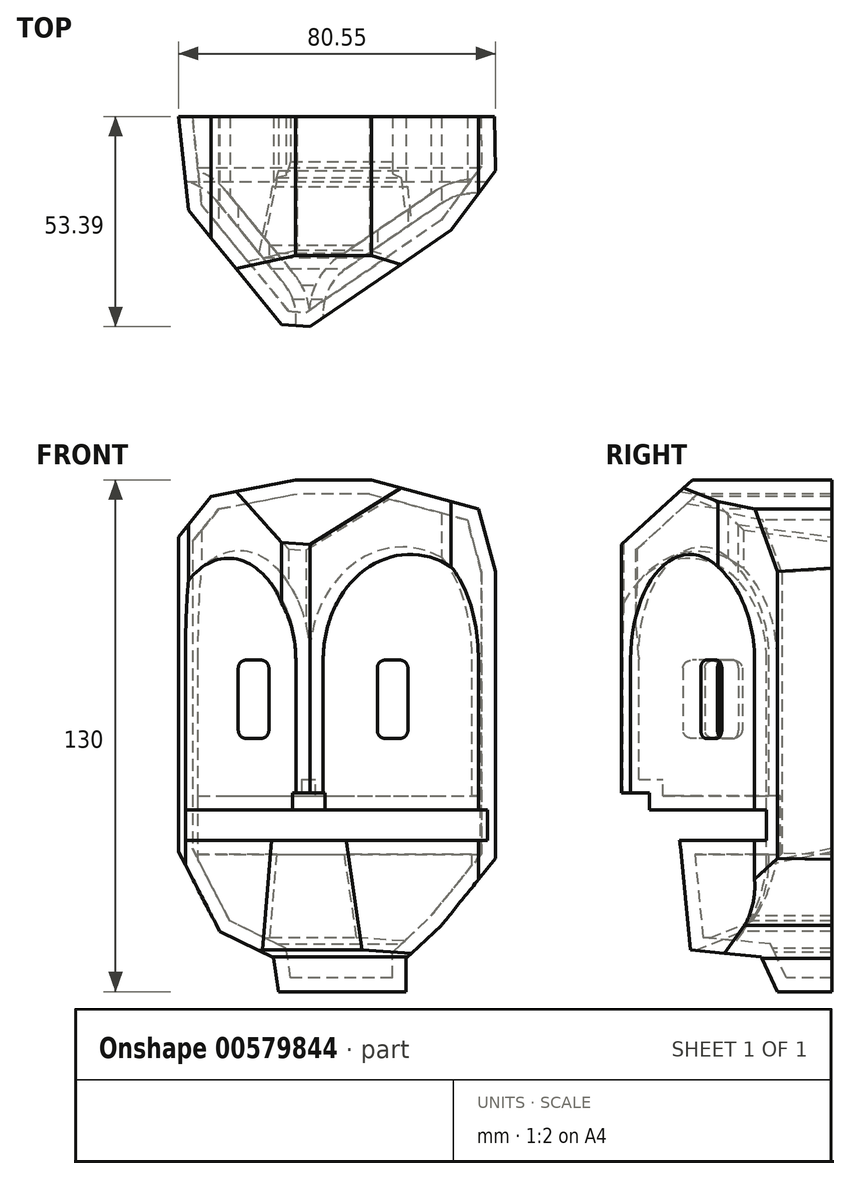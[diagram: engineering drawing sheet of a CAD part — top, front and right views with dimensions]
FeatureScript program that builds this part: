
annotation { "Feature Type Name" : "Feature", "Feature Type Description" : "" }
export const myFeature = defineFeature(function(context is Context, id is Id, definition is map)
    precondition{}
    {
        {
            var Q0;
            Q0=qCreatedBy(makeId("Top.planeOp"),FACE);
            var sketch = newSketch(context, id + "F0", { "sketchPlane" : qUnion([Q0])});
            skLineSegment(sketch, "E0", {"start": v(-31.31, 115.93) * mm, "end": v(-28.8, 92.1) * mm});
            skLineSegment(sketch, "E1", {"start": v(-28.8, 92.1) * mm, "end": v(-5.08, 63.06) * mm});
            skLineSegment(sketch, "E2", {"start": v(-5.08, 63.06) * mm, "end": v(2.1, 62.54) * mm});
            skLineSegment(sketch, "E3", {"start": v(2.1, 62.54) * mm, "end": v(37.94, 87.04) * mm});
            skLineSegment(sketch, "E4", {"start": v(37.94, 87.04) * mm, "end": v(49.24, 102.15) * mm});
            skLineSegment(sketch, "E5", {"start": v(49.24, 102.15) * mm, "end": v(49, 115.93) * mm});
            skLineSegment(sketch, "E6", {"start": v(49, 115.93) * mm, "end": v(-31.31, 115.93) * mm});
            skSolve(sketch);
        }
        {
            var Q0;
            Q0 = qSketchRegion(id + "F0", true);
            extrude(context, id + "F1", {"entities" : qUnion([Q0]), "depth" : 130 * mm, "offsetDistance" : 25 * mm});
        }
        {
            var Q0;
            Q0=makeQuery(id+"F1.opExtrude","SWEPT_FACE",FACE,{"disambiguationData":[OSD([sQuery(id+"F0.wireOp",EDGE,"E3")])]});
            cPlane(context, id + "F2", {"entities" : qUnion([Q0]), "cplaneType" : CPlaneType.OFFSET, "offset" : 13 * mm, "width" : 150 * mm, "height" : 150 * mm});
        }
        {
            var Q0;
            Q0=qCreatedBy(id+"F2.planeOp",FACE);
            var sketch = newSketch(context, id + "F3", { "sketchPlane" : qUnion([Q0])});
            skArc(sketch, "E7", {"start": v(96.46, 84.36) * mm, "mid": v(67.84, 112.98) * mm, "end": v(39.22, 84.36) * mm});
            skLineSegment(sketch, "E8", {"start": v(39.22, -2) * mm, "end": v(39.22, 84.36) * mm});
            skLineSegment(sketch, "E9", {"start": v(96.46, 84.36) * mm, "end": v(96.46, -2) * mm});
            skLineSegment(sketch, "E10", {"start": v(96.46, -2) * mm, "end": v(39.22, -2) * mm});
            skSolve(sketch);
        }
        {
            var Q0;
            Q0 = qSketchRegion(id + "F3", true);
            extrude(context, id + "F4", {"entities" : qUnion([Q0]), "oppositeDirection" : true, "depth" : 20 * mm, "offsetDistance" : 25 * mm});
        }
        {
            var Q0;
            Q0=makeQuery(id+"F4.opExtrude","CAP_EDGE",EDGE,{"disambiguationData":[OSD([sQuery(id+"F3.wireOp",EDGE,"E8")])],"isStart":false});
            fillet(context, id + "F5", {"entities" : qUnion([Q0]), "radius" : 14 * mm, "tangentPropagation" : true, "allowEdgeOverflow" : false});
        }
        {
            var Q0;
            Q0=makeQuery(id+"F4.opExtrude","SWEPT_BODY",BODY,{"disambiguationData":[OSD([sQuery(id+"F3.wireOp",EDGE,"E7"),sQuery(id+"F3.wireOp",EDGE,"E8"),sQuery(id+"F3.wireOp",EDGE,"E9"),sQuery(id+"F3.wireOp",EDGE,"E10")])]});
            var Q1;
            Q1=makeQuery(id+"F1.opExtrude","SWEPT_BODY",BODY,{"disambiguationData":[OSD([sQuery(id+"F0.wireOp",EDGE,"E0"),sQuery(id+"F0.wireOp",EDGE,"E1"),sQuery(id+"F0.wireOp",EDGE,"E2"),sQuery(id+"F0.wireOp",EDGE,"E3"),sQuery(id+"F0.wireOp",EDGE,"E4"),sQuery(id+"F0.wireOp",EDGE,"E5"),sQuery(id+"F0.wireOp",EDGE,"E6")])]});
            booleanBodies(context, id + "F6", {"operationType" : BooleanOperationType.SUBTRACTION, "tools" : qUnion([Q0]), "targets" : qUnion([Q1])});
        }
        {
            var Q0;
            Q0=makeQuery(id+"F1.opExtrude","SWEPT_FACE",FACE,{"disambiguationData":[OSD([sQuery(id+"F0.wireOp",EDGE,"E1")])]});
            cPlane(context, id + "F7", {"entities" : qUnion([Q0]), "cplaneType" : CPlaneType.OFFSET, "offset" : 13 * mm, "width" : 150 * mm, "height" : 150 * mm});
        }
        {
            var Q0;
            Q0=qCreatedBy(id+"F7.planeOp",FACE);
            var sketch = newSketch(context, id + "F8", { "sketchPlane" : qUnion([Q0])});
            skPoint(sketch, "E11.0", {"position": v(-31.54, 84.36) * mm});
            skArc(sketch, "E12", {"start": v(-45.8, 84.36) * mm, "mid": v(-73.43, 112) * mm, "end": v(-101.06, 84.36) * mm});
            skLineSegment(sketch, "E13", {"start": v(-101.06, -2) * mm, "end": v(-101.06, 84.36) * mm});
            skLineSegment(sketch, "E14", {"start": v(-45.8, 84.36) * mm, "end": v(-45.8, -2) * mm});
            skLineSegment(sketch, "E15", {"start": v(-45.8, -2) * mm, "end": v(-101.06, -2) * mm});
            skSolve(sketch);
        }
        {
            var Q0;
            Q0 = qSketchRegion(id + "F8", true);
            extrude(context, id + "F9", {"entities" : qUnion([Q0]), "oppositeDirection" : true, "depth" : 20 * mm, "offsetDistance" : 25 * mm});
        }
        {
            var Q0;
            Q0=makeQuery(id+"F9.opExtrude","CAP_EDGE",EDGE,{"disambiguationData":[OSD([sQuery(id+"F8.wireOp",EDGE,"E12")])],"isStart":false});
            fillet(context, id + "F10", {"entities" : qUnion([Q0]), "radius" : 14 * mm, "tangentPropagation" : true, "allowEdgeOverflow" : false});
        }
        {
            var Q0;
            Q0=makeQuery(id+"F9.opExtrude","SWEPT_BODY",BODY,{"disambiguationData":[OSD([sQuery(id+"F8.wireOp",EDGE,"E12"),sQuery(id+"F8.wireOp",EDGE,"E13"),sQuery(id+"F8.wireOp",EDGE,"E14"),sQuery(id+"F8.wireOp",EDGE,"E15")])]});
            var Q1;
            Q1=makeQuery(id+"F1.opExtrude","SWEPT_BODY",BODY,{"disambiguationData":[OSD([sQuery(id+"F0.wireOp",EDGE,"E0"),sQuery(id+"F0.wireOp",EDGE,"E1"),sQuery(id+"F0.wireOp",EDGE,"E2"),sQuery(id+"F0.wireOp",EDGE,"E3"),sQuery(id+"F0.wireOp",EDGE,"E4"),sQuery(id+"F0.wireOp",EDGE,"E5"),sQuery(id+"F0.wireOp",EDGE,"E6")])]});
            booleanBodies(context, id + "F11", {"operationType" : BooleanOperationType.SUBTRACTION, "tools" : qUnion([Q0]), "targets" : qUnion([Q1])});
        }
        {
            var Q0;
            Q0=qCreatedBy(makeId("Right.planeOp"),FACE);
            var sketch = newSketch(context, id + "F12", { "sketchPlane" : qUnion([Q0])});
            skLineSegment(sketch, "E16.0", {"start": v(62.54, 130) * mm, "end": v(115.93, 130) * mm});
            skLineSegment(sketch, "E16.1", {"start": v(62.54, 130) * mm, "end": v(62.54, 0) * mm});
            skLineSegment(sketch, "E16.2", {"start": v(62.54, 0) * mm, "end": v(115.93, 0) * mm});
            skLineSegment(sketch, "E17", {"start": v(80.56, 130) * mm, "end": v(62.54, 113.63) * mm});
            skLineSegment(sketch, "E18", {"start": v(62.54, 50.45) * mm, "end": v(69.57, 50.45) * mm});
            skLineSegment(sketch, "E19", {"start": v(69.57, 50.45) * mm, "end": v(69.57, 46.2) * mm});
            skLineSegment(sketch, "E20", {"start": v(69.57, 46.2) * mm, "end": v(99.4, 46.2) * mm});
            skLineSegment(sketch, "E21", {"start": v(99.4, 46.2) * mm, "end": v(99.4, 38.43) * mm});
            skLineSegment(sketch, "E22", {"start": v(99.4, 38.43) * mm, "end": v(77.3, 38.43) * mm});
            skLineSegment(sketch, "E23", {"start": v(77.3, 38.43) * mm, "end": v(80.04, 10.6) * mm});
            skLineSegment(sketch, "E24", {"start": v(80.04, 10.6) * mm, "end": v(98.09, 8.8) * mm});
            skLineSegment(sketch, "E25", {"start": v(98.09, 8.8) * mm, "end": v(102.16, 0) * mm});
            skSolve(sketch);
        }
        {
            var Q0;
            {var subQ3=sQuery(id+"F12.wireOp",EDGE,"E17");Q0=makeQuery(id+"F12.imprint","IMPRINT",FACE,{"disambiguationData":[TD([[makeQuery(id+"F12.imprint","IMPRINT",EDGE,{"derivedFrom":subQ3}),-1.0]])]});}
            var Q1;
            {var subQ0=sQuery(id+"F12.wireOp",EDGE,"E18");Q1=makeQuery(id+"F12.imprint","IMPRINT",FACE,{"disambiguationData":[TD([[makeQuery(id+"F12.imprint","IMPRINT",EDGE,{"derivedFrom":subQ0}),-1.0]])]});}
            extrude(context, id + "F13", {"entities" : qUnion([Q0, Q1]), "operationType" : NewBodyOperationType.REMOVE, "oppositeDirection" : true, "depth" : 110 * mm, "offsetDistance" : 25 * mm, "symmetric" : true});
        }
        {
            var Q0;
            Q0=qCreatedBy(makeId("Front.planeOp"),FACE);
            var sketch = newSketch(context, id + "F14", { "sketchPlane" : qUnion([Q0])});
            skPoint(sketch, "E26.0", {"position": v(-31.31, 0) * mm});
            skPoint(sketch, "E26.1", {"position": v(49.24, 0) * mm});
            skPoint(sketch, "E26.2", {"position": v(-31.31, 130) * mm});
            skPoint(sketch, "E26.3", {"position": v(49.24, 130) * mm});
            skLineSegment(sketch, "E27", {"start": v(-31.31, 0) * mm, "end": v(49.24, 0) * mm});
            skLineSegment(sketch, "E28", {"start": v(-31.31, 0) * mm, "end": v(-31.31, 130) * mm});
            skLineSegment(sketch, "E29", {"start": v(-31.31, 130) * mm, "end": v(49.24, 130) * mm});
            skLineSegment(sketch, "E30", {"start": v(49.24, 0) * mm, "end": v(49.24, 130) * mm});
            skLineSegment(sketch, "E31", {"start": v(26.54, 0) * mm, "end": v(26.54, 8.5) * mm});
            skLineSegment(sketch, "E32", {"start": v(26.54, 8.5) * mm, "end": v(35.44, 16.81) * mm});
            skLineSegment(sketch, "E33", {"start": v(35.44, 16.81) * mm, "end": v(49.24, 33.89) * mm});
            skLineSegment(sketch, "E34", {"start": v(-5.84, 0) * mm, "end": v(-7.17, 8.64) * mm});
            skLineSegment(sketch, "E35", {"start": v(-7.17, 8.64) * mm, "end": v(-20.83, 15.33) * mm});
            skLineSegment(sketch, "E36", {"start": v(-20.83, 15.33) * mm, "end": v(-31.31, 35.52) * mm});
            skLineSegment(sketch, "E37", {"start": v(-31.31, 115.54) * mm, "end": v(-23.01, 125.78) * mm});
            skLineSegment(sketch, "E38", {"start": v(-23.01, 125.78) * mm, "end": v(-1.53, 130) * mm});
            skLineSegment(sketch, "E39", {"start": v(17.7, 130) * mm, "end": v(44.91, 122.66) * mm});
            skLineSegment(sketch, "E40", {"start": v(44.91, 122.66) * mm, "end": v(49.24, 106.8) * mm});
            skSolve(sketch);
        }
        {
            var Q0;
            {var subQ3=sQuery(id+"F14.wireOp",EDGE,"E37");Q0=makeQuery(id+"F14.imprint","IMPRINT",FACE,{"disambiguationData":[TD([[makeQuery(id+"F14.imprint","IMPRINT",EDGE,{"derivedFrom":subQ3}),1.0]])]});}
            var Q1;
            {var subQ3=sQuery(id+"F14.wireOp",EDGE,"E39");Q1=makeQuery(id+"F14.imprint","IMPRINT",FACE,{"disambiguationData":[TD([[makeQuery(id+"F14.imprint","IMPRINT",EDGE,{"derivedFrom":subQ3}),1.0]])]});}
            var Q2;
            {var subQ3=sQuery(id+"F14.wireOp",EDGE,"E31");Q2=makeQuery(id+"F14.imprint","IMPRINT",FACE,{"disambiguationData":[TD([[makeQuery(id+"F14.imprint","IMPRINT",EDGE,{"derivedFrom":subQ3}),-1.0]])]});}
            var Q3;
            {var subQ4=sQuery(id+"F14.wireOp",EDGE,"E34");Q3=makeQuery(id+"F14.imprint","IMPRINT",FACE,{"disambiguationData":[TD([[makeQuery(id+"F14.imprint","IMPRINT",EDGE,{"derivedFrom":subQ4}),1.0]])]});}
            extrude(context, id + "F15", {"entities" : qUnion([Q0, Q1, Q2, Q3]), "operationType" : NewBodyOperationType.REMOVE, "oppositeDirection" : true, "depth" : 153 * mm, "offsetDistance" : 25 * mm});
        }
        {
            var Q0;
            Q0=makeQuery(id+"F1.opExtrude","SWEPT_FACE",FACE,{"disambiguationData":[OSD([sQuery(id+"F0.wireOp",EDGE,"E6")])]});
            shell(context, id + "F16", {"entities" : qUnion([Q0]), "thickness" : 3.5 * mm});
        }
        {
            var Q0;
            Q0=qCreatedBy(makeId("Front.planeOp"),FACE);
            var sketch = newSketch(context, id + "F17", { "sketchPlane" : qUnion([Q0])});
            skLineSegment(sketch, "E41.bottom", {"start": v(-14.13, 84.25) * mm, "end": v(-10.36, 84.25) * mm});
            skLineSegment(sketch, "E41.top", {"start": v(-14.13, 64.35) * mm, "end": v(-10.36, 64.35) * mm});
            skLineSegment(sketch, "E41.left", {"start": v(-16.13, 82.25) * mm, "end": v(-16.13, 66.35) * mm});
            skLineSegment(sketch, "E41.right", {"start": v(-8.36, 82.25) * mm, "end": v(-8.36, 66.35) * mm});
            skLineSegment(sketch, "E42.bottom", {"start": v(21.18, 84.25) * mm, "end": v(24.95, 84.25) * mm});
            skLineSegment(sketch, "E42.top", {"start": v(21.18, 64.35) * mm, "end": v(24.95, 64.35) * mm});
            skLineSegment(sketch, "E42.left", {"start": v(19.18, 82.25) * mm, "end": v(19.18, 66.35) * mm});
            skLineSegment(sketch, "E42.right", {"start": v(26.95, 82.25) * mm, "end": v(26.95, 66.35) * mm});
            skPoint(sketch, "E43.visualSharp", {"position": v(-16.13, 84.25) * mm});
            skArc(sketch, "E43.filletArc", {"start": v(-14.13, 84.25) * mm, "mid": v(-15.55, 83.66) * mm, "end": v(-16.13, 82.25) * mm});
            skPoint(sketch, "E44.visualSharp", {"position": v(-8.36, 84.25) * mm});
            skArc(sketch, "E44.filletArc", {"start": v(-8.36, 82.25) * mm, "mid": v(-8.95, 83.66) * mm, "end": v(-10.36, 84.25) * mm});
            skPoint(sketch, "E45.visualSharp", {"position": v(-8.36, 64.35) * mm});
            skArc(sketch, "E45.filletArc", {"start": v(-10.36, 64.35) * mm, "mid": v(-8.95, 64.93) * mm, "end": v(-8.36, 66.35) * mm});
            skPoint(sketch, "E46.visualSharp", {"position": v(-16.13, 64.35) * mm});
            skArc(sketch, "E46.filletArc", {"start": v(-16.13, 66.35) * mm, "mid": v(-15.55, 64.93) * mm, "end": v(-14.13, 64.35) * mm});
            skPoint(sketch, "E47.visualSharp", {"position": v(19.18, 64.35) * mm});
            skArc(sketch, "E47.filletArc", {"start": v(19.18, 66.35) * mm, "mid": v(19.77, 64.93) * mm, "end": v(21.18, 64.35) * mm});
            skPoint(sketch, "E48.visualSharp", {"position": v(26.95, 64.35) * mm});
            skArc(sketch, "E48.filletArc", {"start": v(24.95, 64.35) * mm, "mid": v(26.37, 64.93) * mm, "end": v(26.95, 66.35) * mm});
            skPoint(sketch, "E49.visualSharp", {"position": v(26.95, 84.25) * mm});
            skArc(sketch, "E49.filletArc", {"start": v(26.95, 82.25) * mm, "mid": v(26.37, 83.66) * mm, "end": v(24.95, 84.25) * mm});
            skPoint(sketch, "E50.visualSharp", {"position": v(19.18, 84.25) * mm});
            skArc(sketch, "E50.filletArc", {"start": v(21.18, 84.25) * mm, "mid": v(19.77, 83.66) * mm, "end": v(19.18, 82.25) * mm});
            skSolve(sketch);
        }
        {
            var Q0;
            Q0 = qSketchRegion(id + "F17", true);
            extrude(context, id + "F18", {"entities" : qUnion([Q0]), "operationType" : NewBodyOperationType.REMOVE, "oppositeDirection" : true, "depth" : 95 * mm, "offsetDistance" : 25 * mm});
        }
    });
